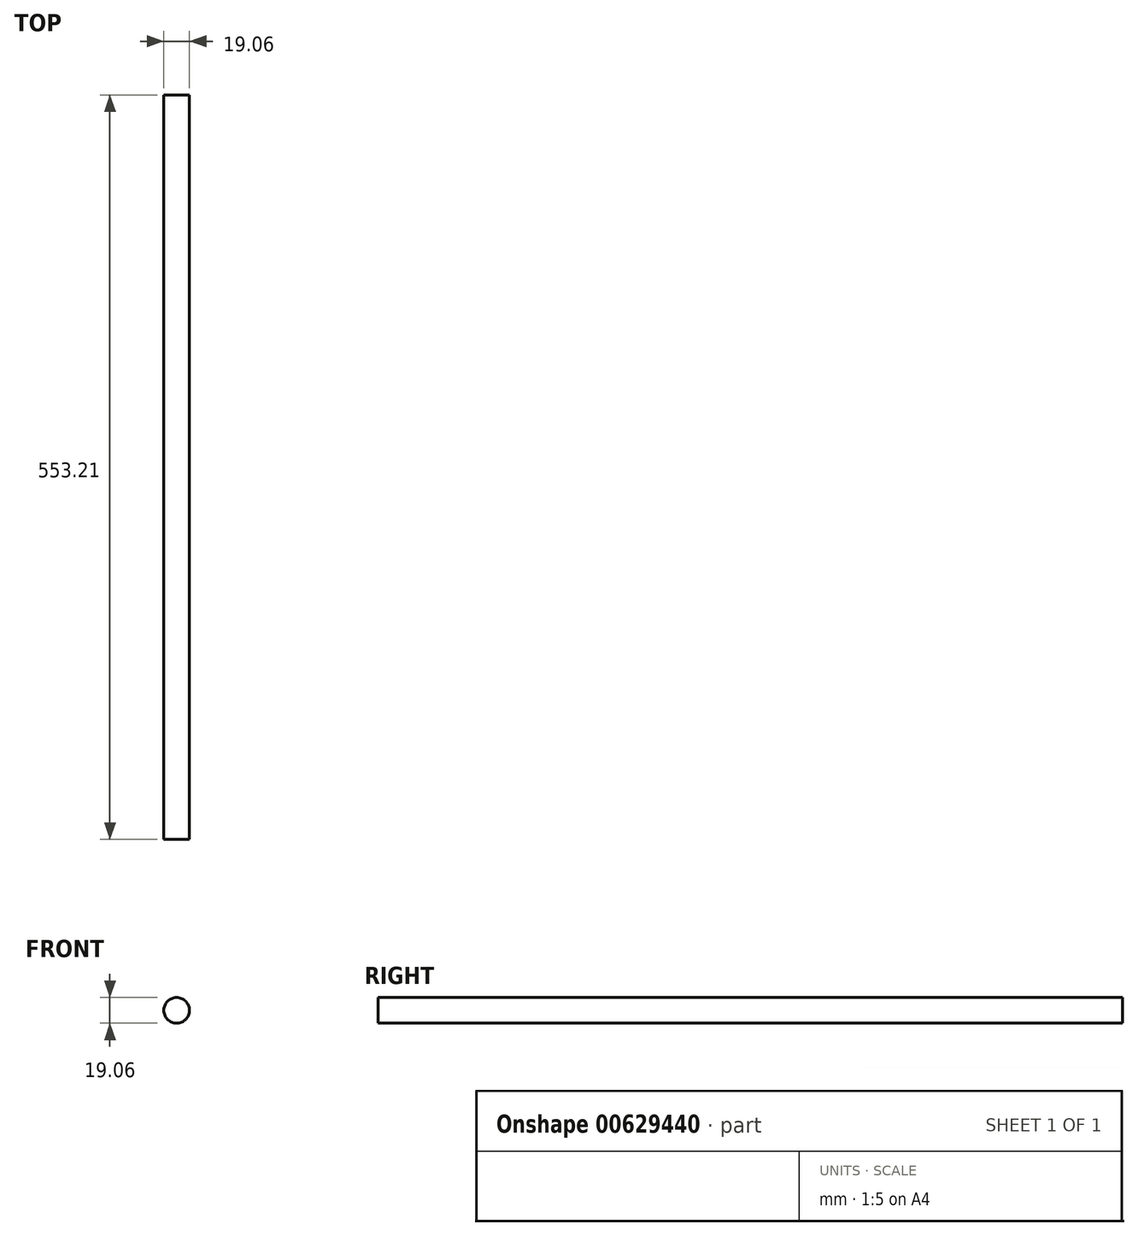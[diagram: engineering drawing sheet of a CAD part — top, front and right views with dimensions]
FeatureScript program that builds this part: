
annotation { "Feature Type Name" : "Feature", "Feature Type Description" : "" }
export const myFeature = defineFeature(function(context is Context, id is Id, definition is map)
    precondition{}
    {
        {
            var Q0;
            Q0=qCreatedBy(makeId("Front.planeOp"),FACE);
            var sketch = newSketch(context, id + "F0", { "sketchPlane" : qUnion([Q0])});
            skCircle(sketch, "E0", {"center": v(0, 0) * mm, "radius": 9.53 * mm});
            skSolve(sketch);
        }
        {
            var Q0;
            Q0=makeQuery(id+"F0.imprint","IMPRINT",FACE,{"disambiguationData":[TD([[makeQuery(id+"F0.imprint","IMPRINT",EDGE,{"derivedFrom":sQuery(id+"F0.wireOp",EDGE,"E0")}),1.0]])]});
            extrude(context, id + "F1", {"entities" : qUnion([Q0]), "oppositeDirection" : true, "depth" : 553.2 * mm, "offsetDistance" : 25.4 * mm});
        }
    });
